# Revit family: Shower-Shower_Door-STERLING-Standard-695B_1
name_source: partatom
category: Specialty Equipment
revit_build: Autodesk Revit 2017 (Build: 20160225_1515(x64)
units: mm (PartAtom-declared; Revit-internal decimal feet)

## family parameters
Cut with Voids When Loaded = No
Host = Face
OmniClass Number = 23.31.17.17
OmniClass Title = Shower Enclosures
Part Type = Normal
Room Calculation Point = No
Round Connector Dimension = Use Diameter
Shared = No

## types (2) — shared parameters
ADA Compliant = No
Assembly Code = C1030200
Date Modified = 07/18/2020
Default Elevation = 0"
Description = Framed sliding shower door, 65inch H x 42 - 48inch W, with 1/8inch thick Hammered glass
Glass Material = Sterling-Glass-G02-Hammered_Glass_Texture
Height = 65"
Length = 2 15/16"
Manufacturer = STERLING Co.
Master Format 2014 = 10 28 19.16
Master Format 2014 Name = Shower Doors
Material = Anodized Aluminum
Product Documentation Link = https://resources.kohler.com
Product Name = Standard
Product Page URL = http://www.sterlingplumbing.com
URL = https://www.sterlingplumbing.com
WaterSense Certified = No

## per-type parameters (varying)
| type | Finish | Model | Type |
| Hammered Glass Texture,S-Silver | Sterling-Metal-S-Silver | 695B-48S-G02 | 1 |
| Hammered Glass Texture,T-Soft Silver | Sterling-Metal-T-Soft_Silver | 695B-48T-G02 | 2 |

## geometry (parser evidence)
native form markers: Sweep x5
no freeform markers — native parametric forms only
